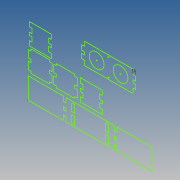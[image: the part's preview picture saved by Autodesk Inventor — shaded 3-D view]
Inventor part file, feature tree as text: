
AUTODESK INVENTOR PART (.ipt)
format: ipt  version: 2020 (Build 240168000, 168)  size: 118,784 bytes
history: native  units: mm
features: sketch x1
ambient origin geometry x8: Origin, YZ Plane, XZ Plane, XY Plane, X Axis, Y Axis, Z Axis, Center Point
feature tree (1):
  sketch  "Sketch1"  dims[d240=3.0mm]
